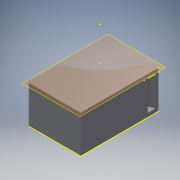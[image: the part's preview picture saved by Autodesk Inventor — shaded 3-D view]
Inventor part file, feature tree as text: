
AUTODESK INVENTOR PART (.ipt)
format: ipt  version: 2016 (Build 200138000, 138)  size: 160,768 bytes
history: native  units: mm
features: sketch x7, reference x5, extrude x3, fillet x3, projected_geometry x2, plane x1, shell x1
ambient origin geometry x8: Origin, YZ Plane, XZ Plane, XY Plane, X Axis, Y Axis, Z Axis, Center Point
bodies: Solid1 (feature_tree)
feature tree (22):
  plane  "Work Plane1"
  extrude  "Extrusion1"  Depth=2.0mm
  sketch  "Sketch2"  dims[d7=2.0mm d8=0.0mm d9=3.0mm d10=5.5mm d13=4.0mm d14=16.0mm d15=0.0mm]
  shell  "Shell1"  Thickness=8.0mm
  extrude  "Extrusion2"  Depth=3.0mm
  sketch  "Sketch4"
  sketch  "Sketch5"
  fillet  "Fillet1"  Radius=5.5mm
  fillet  "Fillet2"  Radius=4.0mm
  fillet  "Fillet5"  Radius=16.0mm
  extrude  "Extrusion3"  [1 undecoded]
  sketch  "Sketch8"
  sketch  "Sketch1"  dims[d0=20.0mm d1=0.0mm d5=2.0mm d6=8.0mm]
  sketch  "Sketch3"
  reference  "Reference1"
  projected_geometry  "Projected Loop1"
  sketch  "Sketch6"
  reference  "Reference2"
  reference  "Reference3"
  reference  "Reference4"
  reference  "Reference5"
  projected_geometry  "Projected Loop2"
note: 1 required parameter value undecoded (feature->parameter linkage not recoverable at this tier; creation-order binding heuristic only, values carry confidence <= 0.55)
